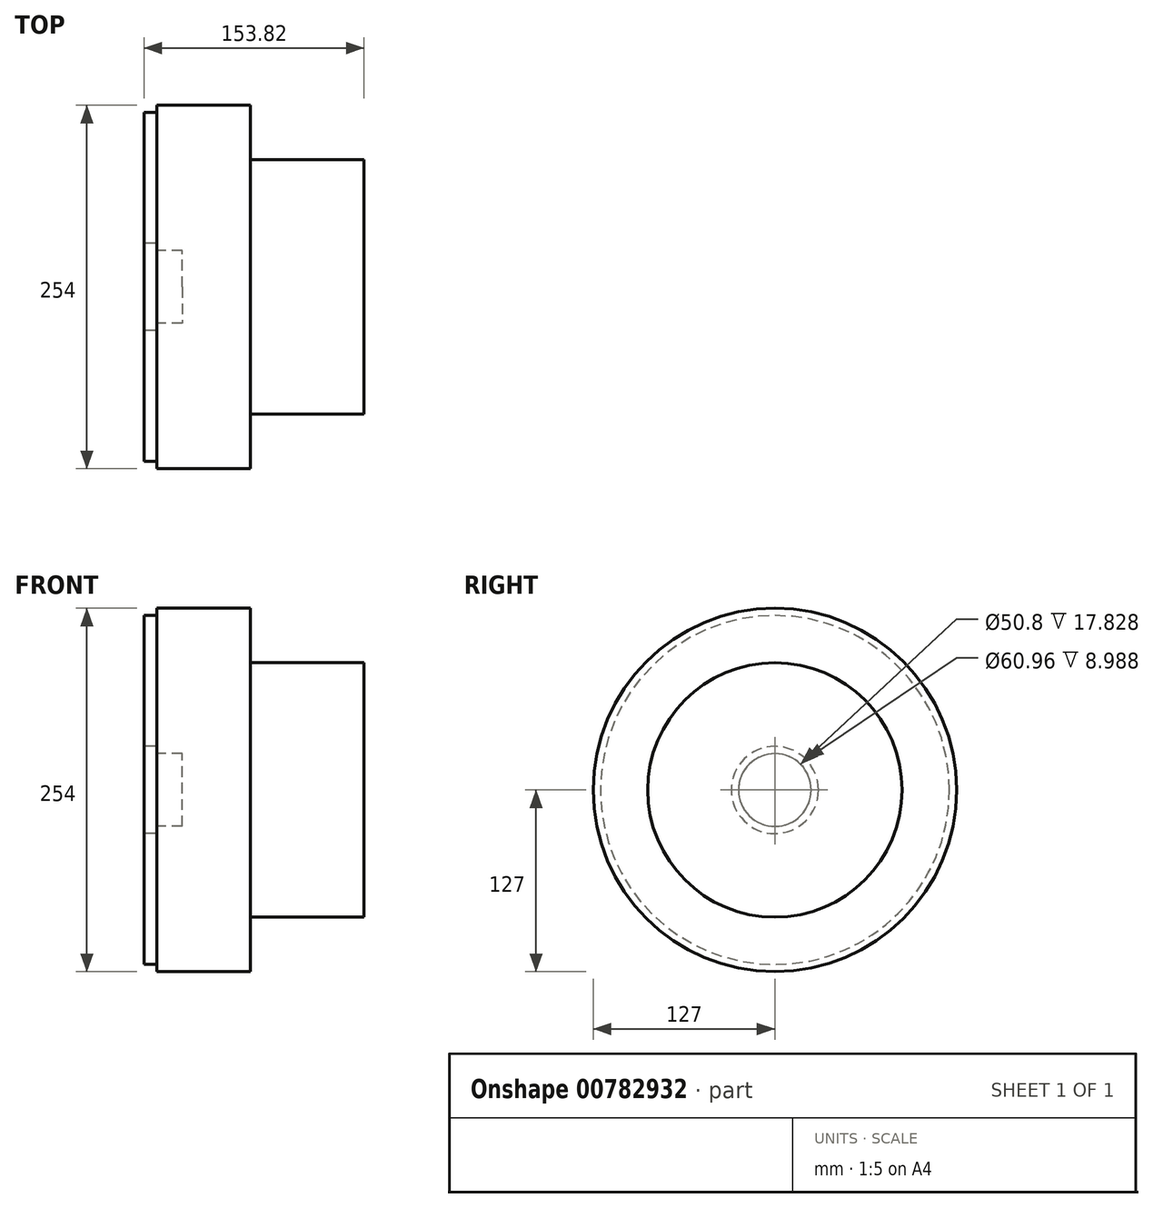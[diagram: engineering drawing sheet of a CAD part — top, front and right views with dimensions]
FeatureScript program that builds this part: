
annotation { "Feature Type Name" : "Feature", "Feature Type Description" : "" }
export const myFeature = defineFeature(function(context is Context, id is Id, definition is map)
    precondition{}
    {
        {
            var Q0;
            Q0=qCreatedBy(makeId("Front.planeOp"),FACE);
            var sketch = newSketch(context, id + "F0", { "sketchPlane" : qUnion([Q0])});
            skLineSegment(sketch, "E0", {"start": v(-76.05, 0) * mm, "end": v(110.74, 0) * mm, "construction": true});
            skLineSegment(sketch, "E1", {"start": v(0, 25.4) * mm, "end": v(55.64, 25.4) * mm});
            skLineSegment(sketch, "E2", {"start": v(55.64, 25.4) * mm, "end": v(55.64, 50.8) * mm});
            skLineSegment(sketch, "E3", {"start": v(55.64, 50.8) * mm, "end": v(47.43, 50.8) * mm});
            skLineSegment(sketch, "E4", {"start": v(47.43, 50.8) * mm, "end": v(47.43, 127) * mm});
            skLineSegment(sketch, "E5", {"start": v(47.43, 127) * mm, "end": v(-17.83, 127) * mm});
            skLineSegment(sketch, "E6", {"start": v(-17.83, 127) * mm, "end": v(-17.83, 121.92) * mm});
            skLineSegment(sketch, "E7", {"start": v(-17.83, 121.92) * mm, "end": v(-26.82, 121.92) * mm});
            skLineSegment(sketch, "E8", {"start": v(-26.82, 121.92) * mm, "end": v(-26.82, 30.48) * mm});
            skLineSegment(sketch, "E9", {"start": v(-26.82, 30.48) * mm, "end": v(-17.83, 30.48) * mm});
            skLineSegment(sketch, "E10", {"start": v(-17.83, 30.48) * mm, "end": v(-17.83, 25.4) * mm});
            skLineSegment(sketch, "E11", {"start": v(-17.83, 25.4) * mm, "end": v(0, 25.4) * mm});
            skSolve(sketch);
        }
        {
            var Q0;
            Q0=makeQuery(id+"F0.imprint","IMPRINT",FACE,{"disambiguationData":[TD([[makeQuery(id+"F0.imprint","IMPRINT",EDGE,{"derivedFrom":sQuery(id+"F0.wireOp",EDGE,"E1")}),1.0]])]});
            var Q1;
            Q1=sQuery(id+"F0.wireOp",EDGE,"E0");
            revolve(context, id + "F1", {"surfaceOperationType" : NewSurfaceOperationType.NEW, "entities" : qUnion([Q0]), "axis" : qUnion([Q1]), "revolveType" : RevolveType.FULL});
        }
        {
            var Q0;
            Q0=qCreatedBy(makeId("Right.planeOp"),FACE);
            var sketch = newSketch(context, id + "F2", { "sketchPlane" : qUnion([Q0])});
            skCircle(sketch, "E12.0", {"center": v(0, 0) * mm, "radius": 88.9 * mm});
            skCircle(sketch, "E13", {"center": v(0, 88.9) * mm, "radius": 12.7 * mm, "construction": true});
            skCircle(sketch, "E14.1.0", {"center": v(-62.86, 62.86) * mm, "radius": 12.7 * mm, "construction": true});
            skCircle(sketch, "E14.2.0", {"center": v(-88.9, 0) * mm, "radius": 12.7 * mm, "construction": true});
            skCircle(sketch, "E14.3.0", {"center": v(-62.86, -62.86) * mm, "radius": 12.7 * mm, "construction": true});
            skCircle(sketch, "E14.4.0", {"center": v(0, -88.9) * mm, "radius": 12.7 * mm, "construction": true});
            skCircle(sketch, "E14.5.0", {"center": v(62.86, -62.86) * mm, "radius": 12.7 * mm, "construction": true});
            skCircle(sketch, "E14.6.0", {"center": v(88.9, 0) * mm, "radius": 12.7 * mm, "construction": true});
            skCircle(sketch, "E14.7.0", {"center": v(62.86, 62.86) * mm, "radius": 12.7 * mm, "construction": true});
            skSolve(sketch);
        }
        {
            var Q0;
            Q0=sQuery(id+"F2.wireOp",EDGE,"E12.0");
            extrude(context, id + "F3", {"bodyType" : ToolBodyType.SURFACE, "surfaceEntities" : qUnion([Q0]), "depth" : 25.4 * mm, "offsetDistance" : 25.4 * mm});
        }
        {
            var Q0;
            Q0 = qSketchRegion(id + "F2", true);
            extrude(context, id + "F4", {"entities" : qUnion([Q0]), "operationType" : NewBodyOperationType.ADD, "depth" : 127 * mm, "offsetDistance" : 25.4 * mm});
        }
    });
